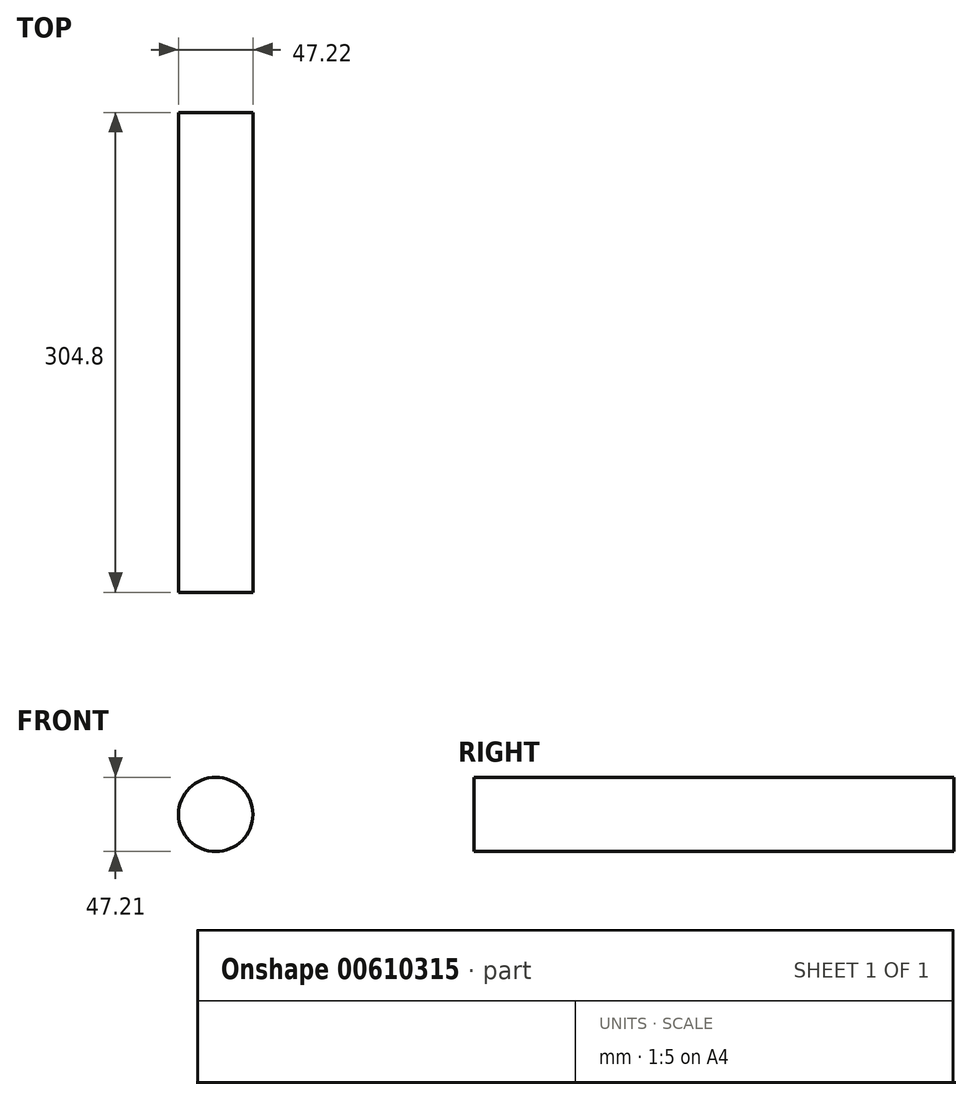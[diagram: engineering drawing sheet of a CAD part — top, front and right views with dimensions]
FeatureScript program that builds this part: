
annotation { "Feature Type Name" : "Feature", "Feature Type Description" : "" }
export const myFeature = defineFeature(function(context is Context, id is Id, definition is map)
    precondition{}
    {
        {
            var Q0;
            Q0=qCreatedBy(makeId("Front.planeOp"),FACE);
            var sketch = newSketch(context, id + "F0", { "sketchPlane" : qUnion([Q0])});
            skCircle(sketch, "E0", {"center": v(47, -39.02) * mm, "radius": 23.6 * mm});
            skCircle(sketch, "E1", {"center": v(47, -39.02) * mm, "radius": 25.4 * mm});
            skSolve(sketch);
        }
        {
            var Q0;
            Q0=makeQuery(id+"F0.imprint","IMPRINT",FACE,{"disambiguationData":[TD([[makeQuery(id+"F0.imprint","IMPRINT",EDGE,{"derivedFrom":sQuery(id+"F0.wireOp",EDGE,"E0")}),1.0]])]});
            extrude(context, id + "F1", {"entities" : qUnion([Q0]), "depth" : 304.8 * mm, "offsetDistance" : 25.4 * mm});
        }
    });
